# Revit family: Урна «Элегант» Арт 7284
name_source: partatom
category: Антураж
revit_build: Autodesk Revit 2018 (Build: 20180423_1000(x64)
units: mm (PartAtom-declared; Revit-internal decimal feet)

## family parameters
Всегда вертикально = Да
Источник визуального образа = Геометрия семейства
На основе рабочей плоскости = Нет
Общий = Нет
При загрузке вырезать с полостями = Нет
Точка расчета площади = Нет

## types (2) — shared parameters
URL = https://hobbyka.ru
Артикул товара = Арт. 7284
Высота = 570 мм
Группа модели = Уличные урны
Длина = 430 мм
Изготовитель = ООО «Хоббика»
Материал изделия = Сталь, дерево
Ширина = 350 мм

## per-type parameters (varying)
| type | Версия «Элегант Нэо» | Версия «Элегант» | Изображение типоразмера | Цвет отделки | Цвет урны |
| Урна «Элегант». Версия «Элегант» | Нет | Да | Урна «Элегант» Арт 7284.jpg | Дерево | Сталь |
| Урна «Элегант». Версия «Элегант Нэо» | Да | Нет | Урна «Элегант» Нэо Арт 7284.jpg | Дерево черненое | Сталь серая |

note: column(s) folded — value = type name in every type: Описание
